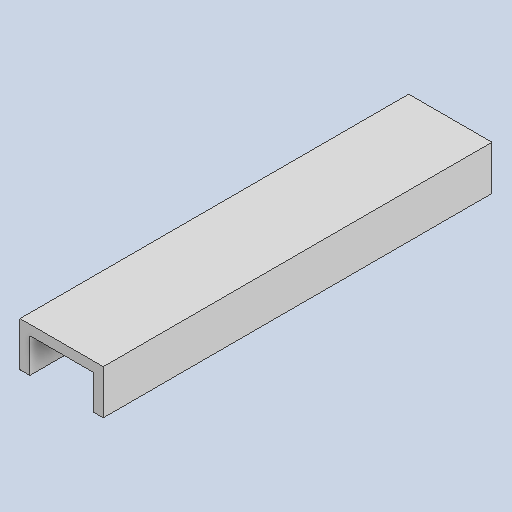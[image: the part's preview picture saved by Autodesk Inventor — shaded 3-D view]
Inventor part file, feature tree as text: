
AUTODESK INVENTOR PART (.ipt)
format: ipt  version: 2023 (Build 270158030, 158C)  size: 90,112 bytes
history: native  units: in
note: dims shown in document units (in); Inventor stores cm internally (conversion verified against a paired STEP export)
features: extrude x1, sketch x1
ambient origin geometry x8: Origin, YZ Plane, XZ Plane, XY Plane, X Axis, Y Axis, Z Axis, Center Point
bodies: Solid1 (feature_tree)
feature tree (2):
  extrude  "Extrusion1"  Depth=1.596in
  sketch  "Sketch1"  dims[d0=3.0in d1=1.596in d2=0.356in d3=0.356in d4=0.356in d5=14.0in d6=0.0in]
